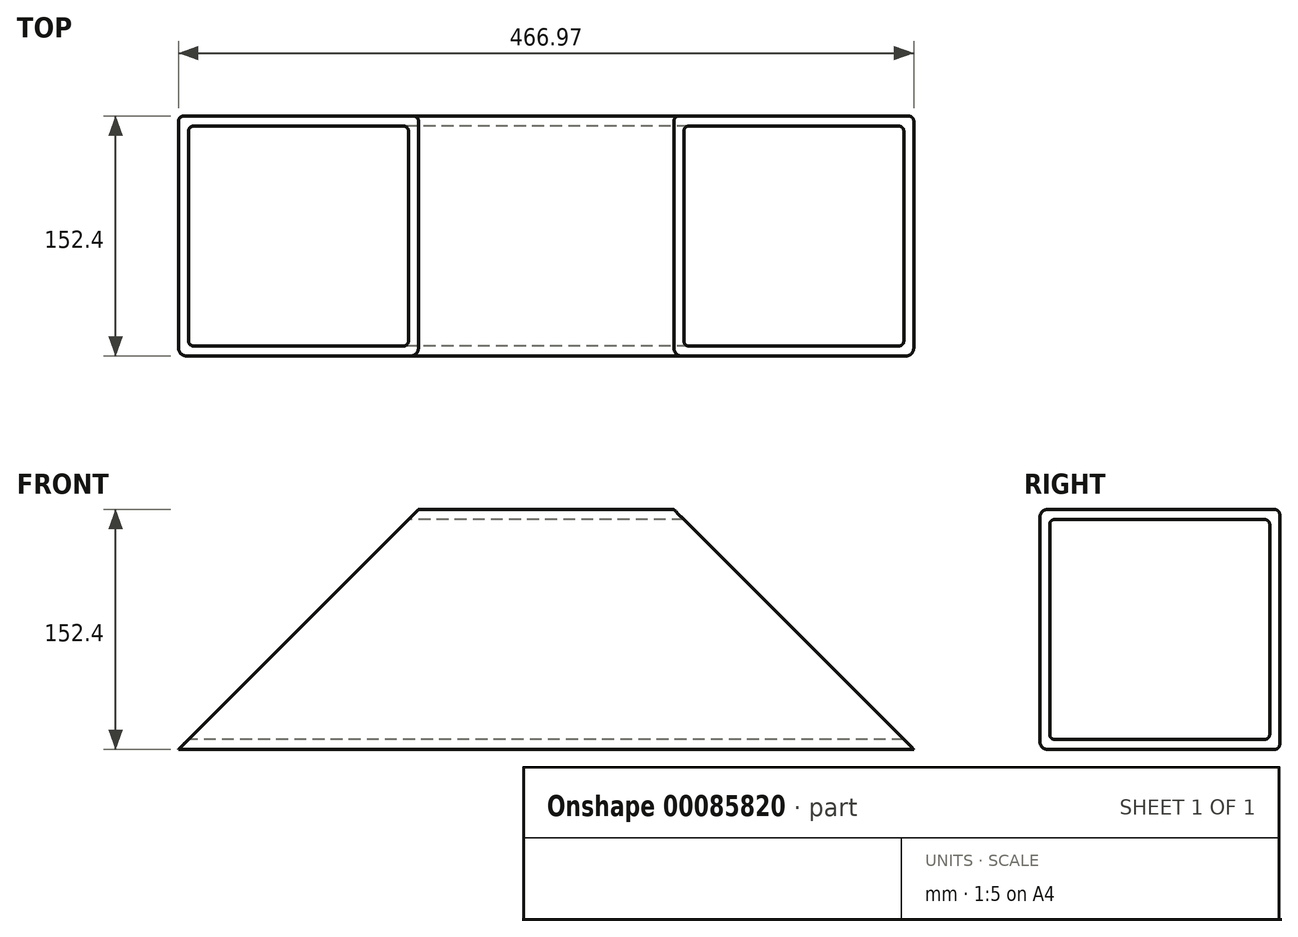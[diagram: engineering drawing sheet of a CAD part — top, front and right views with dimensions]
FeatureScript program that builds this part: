
annotation { "Feature Type Name" : "Feature", "Feature Type Description" : "" }
export const myFeature = defineFeature(function(context is Context, id is Id, definition is map)
    precondition{}
    {
        {
            var Q0;
            Q0=qCreatedBy(makeId("Right.planeOp"),FACE);
            var sketch = newSketch(context, id + "F0", { "sketchPlane" : qUnion([Q0])});
            skLineSegment(sketch, "E0.bottom", {"start": v(-76.2, 76.2) * mm, "end": v(73.03, 76.2) * mm});
            skLineSegment(sketch, "E0.top", {"start": v(-76.2, -76.2) * mm, "end": v(73.02, -76.2) * mm});
            skLineSegment(sketch, "E0.left", {"start": v(-76.2, 76.2) * mm, "end": v(-76.2, -76.2) * mm});
            skLineSegment(sketch, "E0.right", {"start": v(76.2, 73.02) * mm, "end": v(76.2, -73.03) * mm});
            skPoint(sketch, "E0.middle", {"position": v(0, 0) * mm});
            skLineSegment(sketch, "E1.0", {"start": v(-69.85, 66.68) * mm, "end": v(-69.85, -66.67) * mm});
            skLineSegment(sketch, "E2.3", {"start": v(-66.68, -69.85) * mm, "end": v(66.68, -69.85) * mm});
            skLineSegment(sketch, "E3.0", {"start": v(69.85, 66.68) * mm, "end": v(69.85, -66.67) * mm});
            skLineSegment(sketch, "E3.1", {"start": v(-66.68, 69.85) * mm, "end": v(66.68, 69.85) * mm});
            skPoint(sketch, "E4.visualSharp", {"position": v(-76.2, 76.2) * mm});
            skPoint(sketch, "E5.visualSharp", {"position": v(76.2, 76.2) * mm});
            skArc(sketch, "E5.filletArc", {"start": v(76.2, 73.02) * mm, "mid": v(75.27, 75.27) * mm, "end": v(73.03, 76.2) * mm});
            skPoint(sketch, "E6.visualSharp", {"position": v(76.2, -76.2) * mm});
            skArc(sketch, "E6.filletArc", {"start": v(73.02, -76.2) * mm, "mid": v(75.27, -75.27) * mm, "end": v(76.2, -73.03) * mm});
            skPoint(sketch, "E7.visualSharp", {"position": v(-76.2, -76.2) * mm});
            skPoint(sketch, "E8.visualSharp", {"position": v(-69.85, -69.85) * mm});
            skArc(sketch, "E8.filletArc", {"start": v(-69.85, -66.67) * mm, "mid": v(-68.92, -68.92) * mm, "end": v(-66.68, -69.85) * mm});
            skPoint(sketch, "E9.visualSharp", {"position": v(-69.85, 69.85) * mm});
            skArc(sketch, "E9.filletArc", {"start": v(-66.68, 69.85) * mm, "mid": v(-68.92, 68.92) * mm, "end": v(-69.85, 66.68) * mm});
            skPoint(sketch, "E10.visualSharp", {"position": v(69.85, 69.85) * mm});
            skArc(sketch, "E10.filletArc", {"start": v(69.85, 66.68) * mm, "mid": v(68.92, 68.92) * mm, "end": v(66.68, 69.85) * mm});
            skPoint(sketch, "E11.visualSharp", {"position": v(69.85, -69.85) * mm});
            skArc(sketch, "E11.filletArc", {"start": v(66.68, -69.85) * mm, "mid": v(68.92, -68.92) * mm, "end": v(69.85, -66.67) * mm});
            skSolve(sketch);
        }
        {
            var Q0;
            Q0=makeQuery(id+"F0.imprint","IMPRINT",FACE,{"disambiguationData":[TD([[makeQuery(id+"F0.imprint","IMPRINT",EDGE,{"derivedFrom":sQuery(id+"F0.wireOp",EDGE,"E0.bottom")}),-1.0]])]});
            extrude(context, id + "F1", {"entities" : qUnion([Q0]), "depth" : 466.97 * mm, "offsetDistance" : 25.4 * mm});
        }
        {
            var Q0;
            Q0=makeQuery(id+"F1.opExtrude","SWEPT_FACE",FACE,{"disambiguationData":[OSD([sQuery(id+"F0.wireOp",EDGE,"E0.left")])]});
            var sketch = newSketch(context, id + "F2", { "sketchPlane" : qUnion([Q0])});
            skLineSegment(sketch, "E12", {"start": v(0, -76.2) * mm, "end": v(152.4, 76.2) * mm});
            skLineSegment(sketch, "E13", {"start": v(466.97, -76.2) * mm, "end": v(314.57, 76.2) * mm});
            skSolve(sketch);
        }
        {
            var Q0;
            {var subQ0=sQuery(id+"F2.wireOp",EDGE,"E12");Q0=makeQuery(id+"F2.imprint","IMPRINT",FACE,{"disambiguationData":[TD([[makeQuery(id+"F2.imprint","IMPRINT",EDGE,{"derivedFrom":subQ0}),1.0]])]});}
            var Q1;
            {var subQ0=sQuery(id+"F2.wireOp",EDGE,"E13");Q1=makeQuery(id+"F2.imprint","IMPRINT",FACE,{"disambiguationData":[TD([[makeQuery(id+"F2.imprint","IMPRINT",EDGE,{"derivedFrom":subQ0}),-1.0]])]});}
            extrude(context, id + "F3", {"entities" : qUnion([Q0, Q1]), "operationType" : NewBodyOperationType.REMOVE, "endBound" : BoundingType.THROUGH_ALL, "oppositeDirection" : true, "depth" : 25.4 * mm, "offsetDistance" : 25.4 * mm});
        }
        {
            var Q0;
            Q0=makeQuery(id+"F1.opExtrude","SWEPT_EDGE",EDGE,{"disambiguationData":[OSD([sQuery(id+"F0.wireOp",EDGE,"E0.bottom"),sQuery(id+"F0.wireOp",EDGE,"E0.left")])]});
            var Q1;
            Q1=makeQuery(id+"F1.opExtrude","SWEPT_EDGE",EDGE,{"disambiguationData":[OSD([sQuery(id+"F0.wireOp",EDGE,"E0.top"),sQuery(id+"F0.wireOp",EDGE,"E0.left")])]});
            fillet(context, id + "F4", {"entities" : qUnion([Q0, Q1]), "radius" : 5.08 * mm, "tangentPropagation" : true, "allowEdgeOverflow" : false});
        }
    });
